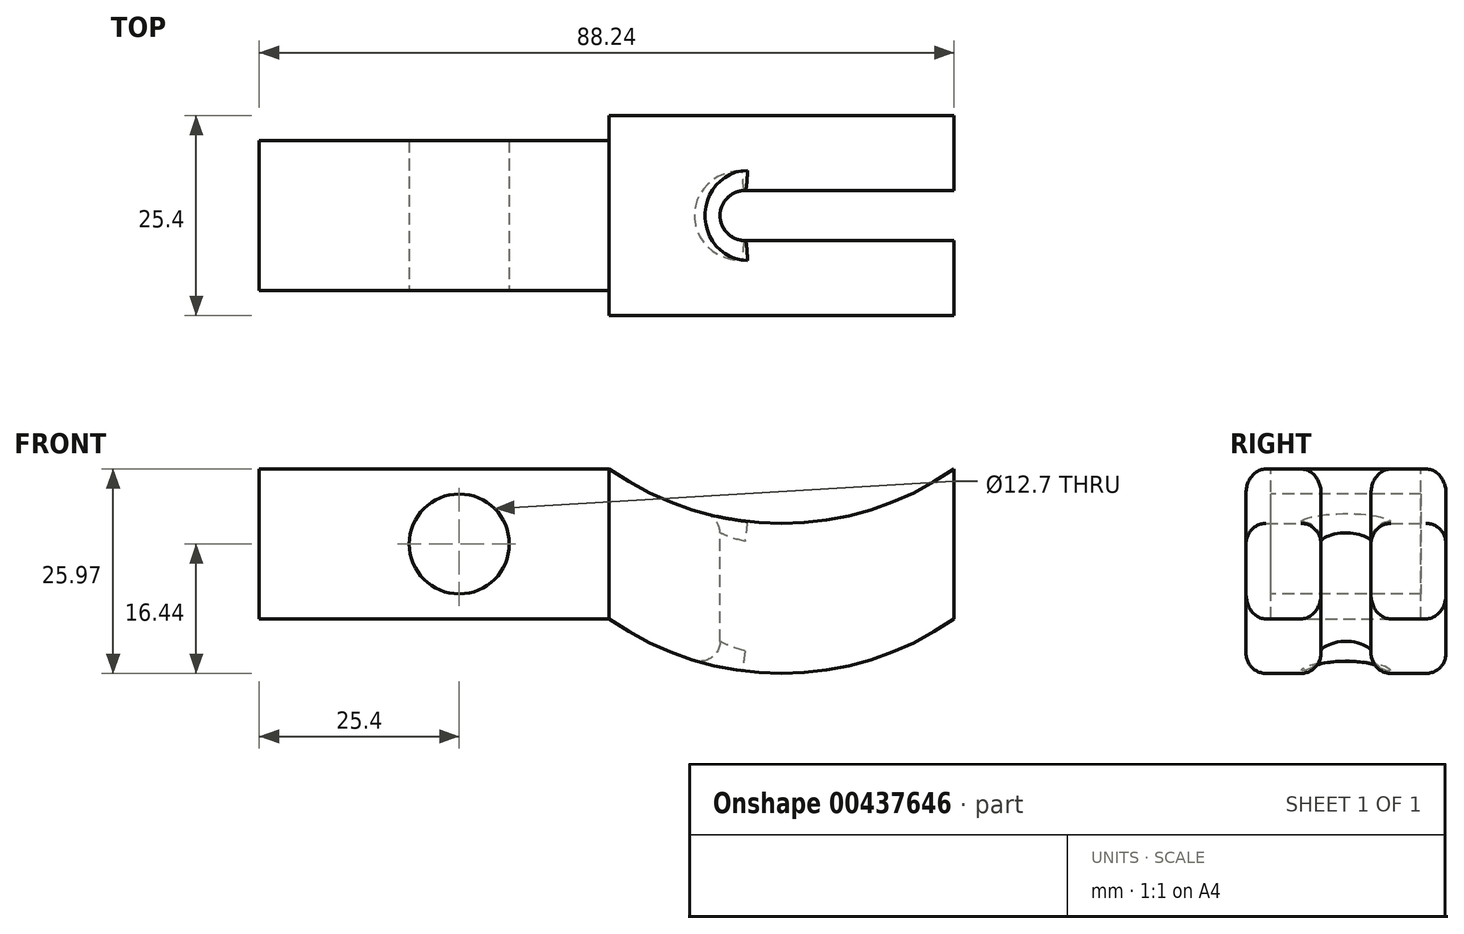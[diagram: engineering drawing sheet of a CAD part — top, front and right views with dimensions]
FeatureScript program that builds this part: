
annotation { "Feature Type Name" : "Feature", "Feature Type Description" : "" }
export const myFeature = defineFeature(function(context is Context, id is Id, definition is map)
    precondition{}
    {
        {
            var Q0;
            Q0=qCreatedBy(makeId("Front.planeOp"),FACE);
            var sketch = newSketch(context, id + "F0", { "sketchPlane" : qUnion([Q0])});
            skLineSegment(sketch, "E0.left", {"start": v(-19.49, 0) * mm, "end": v(-19.49, -19.05) * mm});
            skLineSegment(sketch, "E0.right", {"start": v(24.3, 0) * mm, "end": v(24.3, -19.05) * mm});
            skArc(sketch, "E1", {"start": v(-19.49, 0) * mm, "mid": v(2.4, -6.92) * mm, "end": v(24.3, 0) * mm});
            skArc(sketch, "E2", {"start": v(-19.49, -19.05) * mm, "mid": v(2.4, -25.97) * mm, "end": v(24.3, -19.05) * mm});
            skSolve(sketch);
        }
        {
            var Q0;
            Q0 = qSketchRegion(id + "F0", true);
            extrude(context, id + "F1", {"entities" : qUnion([Q0]), "depth" : 25.4 * mm});
        }
        {
            var Q0;
            Q0=qCreatedBy(makeId("Top.planeOp"),FACE);
            var sketch = newSketch(context, id + "F2", { "sketchPlane" : qUnion([Q0])});
            skLineSegment(sketch, "E3", {"start": v(26.97, -9.53) * mm, "end": v(-2.24, -9.53) * mm});
            skArc(sketch, "E4", {"start": v(-2.24, -9.53) * mm, "mid": v(-5.42, -12.7) * mm, "end": v(-2.24, -15.88) * mm});
            skLineSegment(sketch, "E5", {"start": v(-2.24, -15.88) * mm, "end": v(26.97, -15.88) * mm});
            skLineSegment(sketch, "E6", {"start": v(26.97, -9.53) * mm, "end": v(26.97, -15.88) * mm});
            skLineSegment(sketch, "E7", {"start": v(26.97, 0) * mm, "end": v(26.97, -9.53) * mm});
            skLineSegment(sketch, "E8", {"start": v(26.97, -15.88) * mm, "end": v(26.97, -25.4) * mm});
            skSolve(sketch);
        }
        {
            var Q0;
            Q0 = qSketchRegion(id + "F2", true);
            extrude(context, id + "F3", {"entities" : qUnion([Q0]), "operationType" : NewBodyOperationType.REMOVE, "endBound" : BoundingType.THROUGH_ALL, "oppositeDirection" : true, "depth" : 25.4 * mm});
        }
        {
            var Q0;
            Q0=makeQuery(id+"F1.opExtrude","SWEPT_FACE",FACE,{"disambiguationData":[OSD([sQuery(id+"F0.wireOp",EDGE,"E0.left")])]});
            var sketch = newSketch(context, id + "F4", { "sketchPlane" : qUnion([Q0])});
            skLineSegment(sketch, "E9.bottom", {"start": v(3.18, -19.05) * mm, "end": v(22.23, -19.05) * mm});
            skLineSegment(sketch, "E9.top", {"start": v(3.18, 0) * mm, "end": v(22.23, 0) * mm});
            skLineSegment(sketch, "E9.left", {"start": v(3.18, -19.05) * mm, "end": v(3.18, 0) * mm});
            skLineSegment(sketch, "E9.right", {"start": v(22.23, -19.05) * mm, "end": v(22.23, 0) * mm});
            skSolve(sketch);
        }
        {
            var Q0;
            Q0 = qSketchRegion(id + "F4", true);
            extrude(context, id + "F5", {"entities" : qUnion([Q0]), "operationType" : NewBodyOperationType.ADD, "depth" : 44.45 * mm});
        }
        {
            var Q0;
            Q0=makeQuery(id+"F1.opExtrude","CAP_EDGE",EDGE,{"disambiguationData":[OSD([sQuery(id+"F0.wireOp",EDGE,"E2")])],"isStart":false});
            var Q1;
            Q1=makeQuery(id+"F1.opExtrude","CAP_EDGE",EDGE,{"disambiguationData":[OSD([sQuery(id+"F0.wireOp",EDGE,"E1")])],"isStart":false});
            var Q2;
            Q2=makeQuery(id+"F1.opExtrude","CAP_EDGE",EDGE,{"disambiguationData":[OSD([sQuery(id+"F0.wireOp",EDGE,"E1")])],"isStart":true});
            var Q3;
            Q3=makeQuery(id+"F1.opExtrude","CAP_EDGE",EDGE,{"disambiguationData":[OSD([sQuery(id+"F0.wireOp",EDGE,"E2")])],"isStart":true});
            var Q4;
            Q4=makeQuery(id+"F3.boolean.opBoolean","INTERSECT",EDGE,{"derivedFrom":[makeQuery(id+"F1.opExtrude","SWEPT_FACE",FACE,{"disambiguationData":[OSD([sQuery(id+"F0.wireOp",EDGE,"E2")])]}),makeQuery(id+"F3.opExtrude","SWEPT_FACE",FACE,{"disambiguationData":[OSD([sQuery(id+"F2.wireOp",EDGE,"E3")])]})]});
            var Q5;
            Q5=makeQuery(id+"F3.boolean.opBoolean","INTERSECT",EDGE,{"derivedFrom":[makeQuery(id+"F1.opExtrude","SWEPT_FACE",FACE,{"disambiguationData":[OSD([sQuery(id+"F0.wireOp",EDGE,"E2")])]}),makeQuery(id+"F3.opExtrude","SWEPT_FACE",FACE,{"disambiguationData":[OSD([sQuery(id+"F2.wireOp",EDGE,"E5")])]})]});
            var Q6;
            Q6=makeQuery(id+"F3.boolean.opBoolean","INTERSECT",EDGE,{"derivedFrom":[makeQuery(id+"F1.opExtrude","SWEPT_FACE",FACE,{"disambiguationData":[OSD([sQuery(id+"F0.wireOp",EDGE,"E1")])]}),makeQuery(id+"F3.opExtrude","SWEPT_FACE",FACE,{"disambiguationData":[OSD([sQuery(id+"F2.wireOp",EDGE,"E3")])]})]});
            var Q7;
            Q7=makeQuery(id+"F3.boolean.opBoolean","INTERSECT",EDGE,{"derivedFrom":[makeQuery(id+"F1.opExtrude","SWEPT_FACE",FACE,{"disambiguationData":[OSD([sQuery(id+"F0.wireOp",EDGE,"E1")])]}),makeQuery(id+"F3.opExtrude","SWEPT_FACE",FACE,{"disambiguationData":[OSD([sQuery(id+"F2.wireOp",EDGE,"E5")])]})]});
            fillet(context, id + "F6", {"entities" : qUnion([Q0, Q1, Q2, Q3, Q4, Q5, Q6, Q7]), "radius" : 2.54 * mm, "tangentPropagation" : true, "allowEdgeOverflow" : false});
        }
        {
            var Q0;
            Q0=makeQuery(id+"F5.opExtrude","SWEPT_FACE",FACE,{"disambiguationData":[OSD([sQuery(id+"F4.wireOp",EDGE,"E9.right")])]});
            var sketch = newSketch(context, id + "F7", { "sketchPlane" : qUnion([Q0])});
            skLineSegment(sketch, "E10.bottom", {"start": v(-63.94, 0) * mm, "end": v(-38.54, 0) * mm});
            skLineSegment(sketch, "E10.top", {"start": v(-63.94, -9.53) * mm, "end": v(-38.54, -9.53) * mm});
            skLineSegment(sketch, "E10.left", {"start": v(-63.94, 0) * mm, "end": v(-63.94, -9.53) * mm});
            skLineSegment(sketch, "E10.right", {"start": v(-38.54, 0) * mm, "end": v(-38.54, -9.53) * mm});
            skSolve(sketch);
        }
        {
            var Q0;
            Q0=sQuery(id+"F7.wireOp",VERTEX,"E10.right.end");
            var Q1;
            Q1=makeQuery(id+"F1.opExtrude","SWEPT_BODY",BODY,{"disambiguationData":[OSD([sQuery(id+"F0.wireOp",EDGE,"E0.right"),sQuery(id+"F0.wireOp",EDGE,"E1"),sQuery(id+"F0.wireOp",EDGE,"E0.left"),sQuery(id+"F0.wireOp",EDGE,"E2")])]});
            hole(context, id + "F8", {"style" : HoleStyle.SIMPLE, "endStyle" : HoleEndStyle.THROUGH, "holeDiameter" : 12.7 * mm, "isTappedThrough" : true, "tappedDepth" : 12.7 * mm, "tapClearance" : 3, "startFromSketch" : true, "locations" : qUnion([Q0]), "scope" : qUnion([Q1])});
        }
    });
